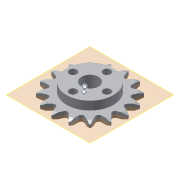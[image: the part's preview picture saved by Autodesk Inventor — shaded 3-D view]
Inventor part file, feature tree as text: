
AUTODESK INVENTOR PART (.ipt)
format: ipt  version: 2013 (Build 170138000, 138)  size: 416,768 bytes
history: native  units: in
note: dims shown in document units (in); Inventor stores cm internally (conversion verified against a paired STEP export)
features: other x17, plane x1
ambient origin geometry x8: Origin, YZ Plane, XZ Plane, XY Plane, X Axis, Y Axis, Z Axis, Center Point
bodies: Solid1 (feature_tree)
feature tree (18):
  other  "Tetrix sprocket 16T.ipt"
  other  "sprocket_25_16t_tetrix::Tetrix sprocket 16T.ipt"
  other  "TaggingFeature1"
  other  "FRONT"
  other  "TOP"
  other  "RIGHT"
  plane  "Work Plane4"
  other  "A_1"
  other  "A_2"
  other  "A_4"
  other  "A_5"
  other  "A_6"
  other  "A_3"
  other  "A_7"
  other  "A_8"
  other  "A_9"
  other  "iComposite:2"
  other  "iComposite:1"
